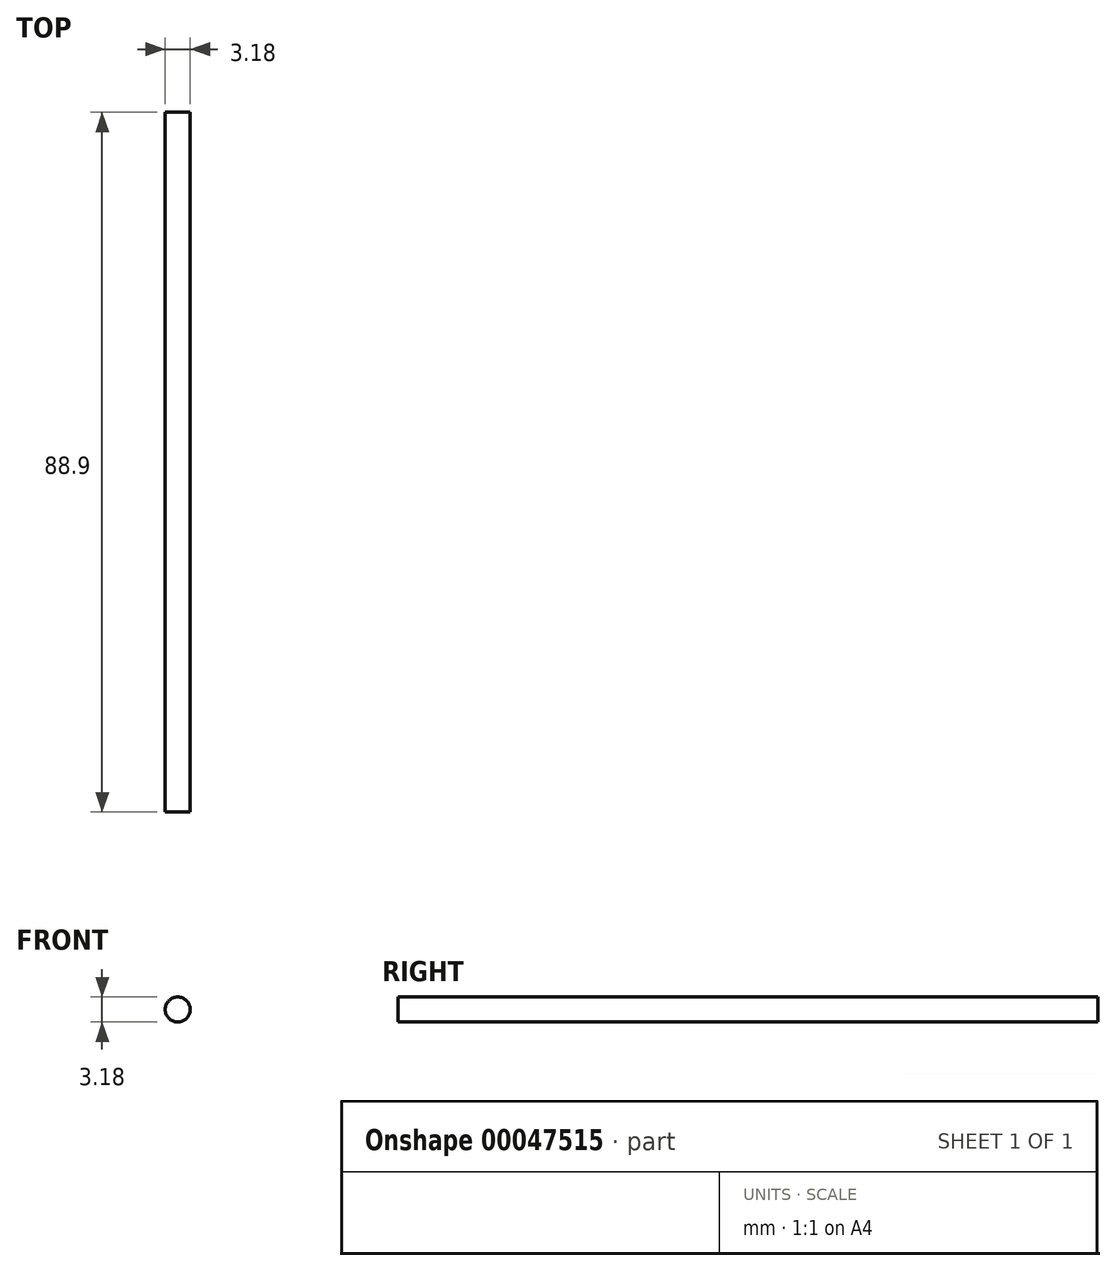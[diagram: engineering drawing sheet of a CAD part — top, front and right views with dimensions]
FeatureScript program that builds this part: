
annotation { "Feature Type Name" : "Feature", "Feature Type Description" : "" }
export const myFeature = defineFeature(function(context is Context, id is Id, definition is map)
    precondition{}
    {
        {
            var Q0;
            Q0=qCreatedBy(makeId("Front.planeOp"),FACE);
            var sketch = newSketch(context, id + "F0", { "sketchPlane" : qUnion([Q0])});
            skCircle(sketch, "E0", {"center": v(0, 0) * mm, "radius": 1.59 * mm});
            skSolve(sketch);
        }
        {
            var Q0;
            Q0=makeQuery(id+"F0.imprint","IMPRINT",FACE,{"disambiguationData":[TD([[makeQuery(id+"F0.imprint","IMPRINT",EDGE,{"derivedFrom":sQuery(id+"F0.wireOp",EDGE,"E0")}),1.0]])]});
            extrude(context, id + "F1", {"entities" : qUnion([Q0]), "endBound" : BoundingType.SYMMETRIC, "depth" : 88.9 * mm});
        }
    });
